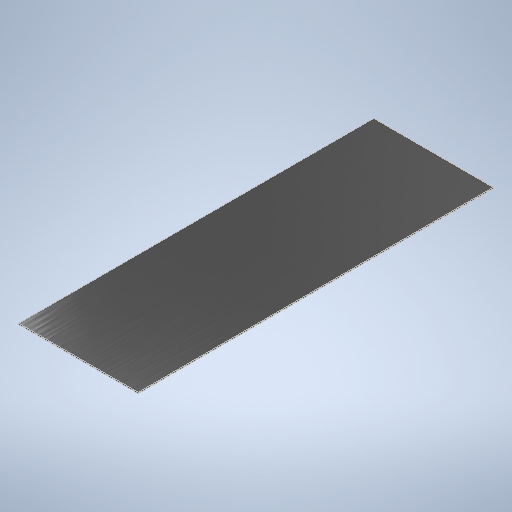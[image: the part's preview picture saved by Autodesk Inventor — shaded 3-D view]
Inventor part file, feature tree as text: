
AUTODESK INVENTOR PART (.ipt)
format: ipt  version: 2025.1 (Build 291241020, 241B)  size: 238,080 bytes
history: native  units: in
note: dims shown in document units (in); Inventor stores cm internally (conversion verified against a paired STEP export)
features: extrude x1, sketch x1
ambient origin geometry x8: Origin, YZ Plane, XZ Plane, XY Plane, X Axis, Y Axis, Z Axis, Center Point
bodies: Solid1 (feature_tree)
feature tree (2):
  extrude  "Extrusion1"  Depth=39.375in
  sketch  "Sketch1"  dims[d0=13.25in d1=39.375in d2=0.125in d3=0.0in]
